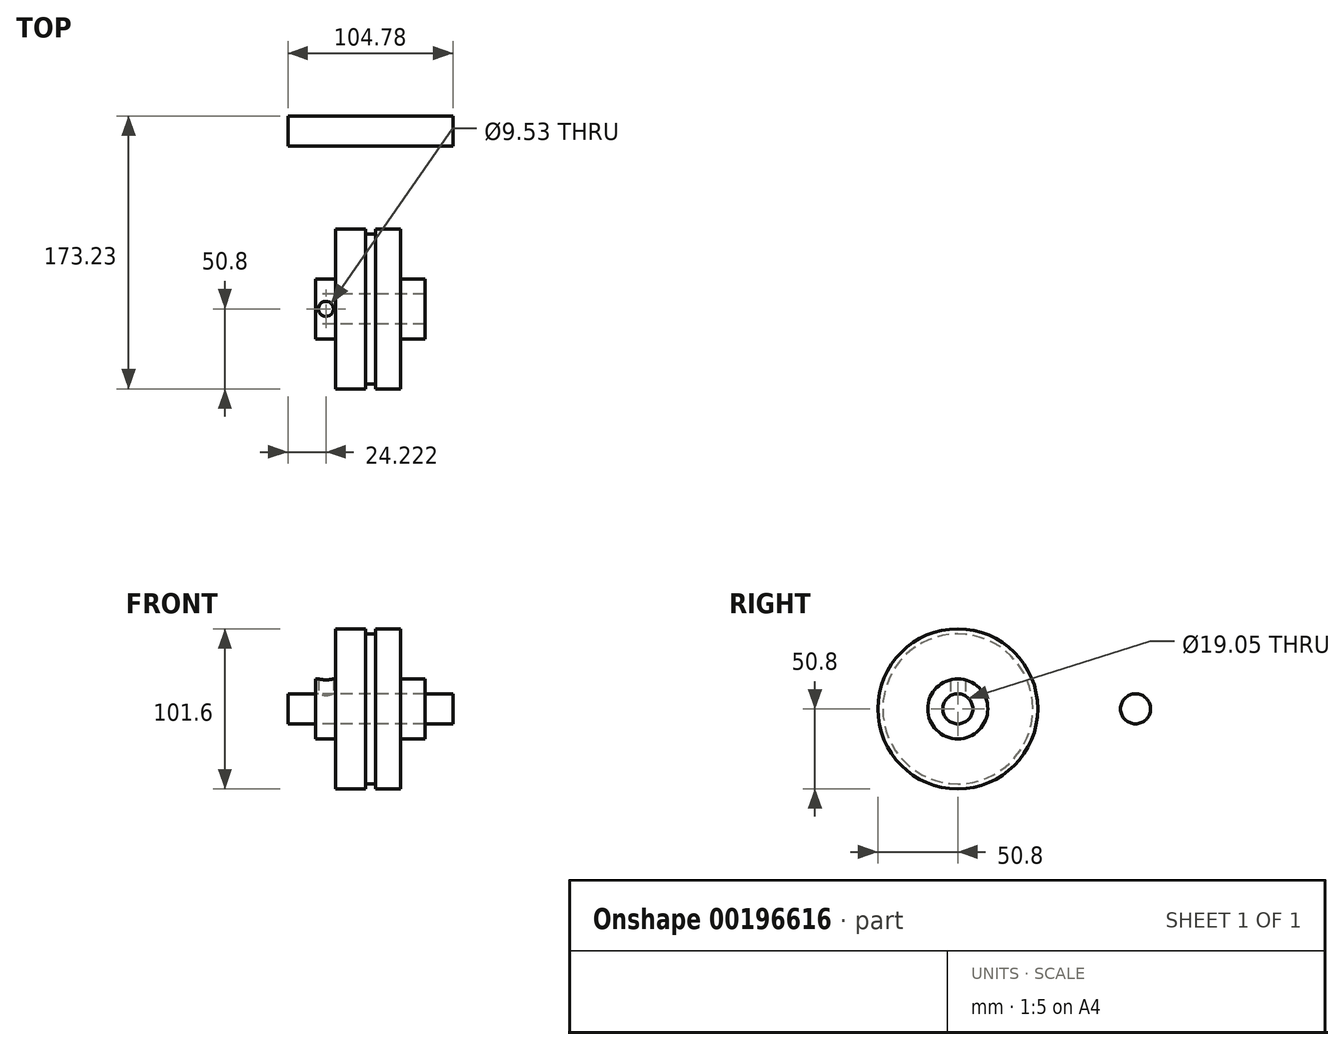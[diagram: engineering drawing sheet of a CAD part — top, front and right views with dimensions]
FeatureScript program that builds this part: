
annotation { "Feature Type Name" : "Feature", "Feature Type Description" : "" }
export const myFeature = defineFeature(function(context is Context, id is Id, definition is map)
    precondition{}
    {
        {
            var Q0;
            Q0=qCreatedBy(makeId("Right.planeOp"),FACE);
            var sketch = newSketch(context, id + "F0", { "sketchPlane" : qUnion([Q0])});
            skCircle(sketch, "E0", {"center": v(0, 0) * mm, "radius": 9.53 * mm});
            skCircle(sketch, "E1", {"center": v(0, 0) * mm, "radius": 19.05 * mm});
            skSolve(sketch);
        }
        {
            var Q0;
            Q0=qCreatedBy(makeId("Right.planeOp"),FACE);
            var sketch = newSketch(context, id + "F1", { "sketchPlane" : qUnion([Q0])});
            skCircle(sketch, "E2", {"center": v(112.9, 0) * mm, "radius": 9.53 * mm});
            skSolve(sketch);
        }
        {
            var Q0;
            Q0=makeQuery(id+"F0.imprint","IMPRINT",FACE,{"disambiguationData":[TD([[makeQuery(id+"F0.imprint","IMPRINT",EDGE,{"derivedFrom":sQuery(id+"F0.wireOp",EDGE,"E0")}),-1.0]])]});
            extrude(context, id + "F2", {"entities" : qUnion([Q0]), "endBound" : BoundingType.SYMMETRIC, "depth" : 69.34 * mm});
        }
        {
            var Q0;
            Q0=qCreatedBy(makeId("Right.planeOp"),FACE);
            var sketch = newSketch(context, id + "F3", { "sketchPlane" : qUnion([Q0])});
            skCircle(sketch, "E3", {"center": v(0, 0) * mm, "radius": 50.8 * mm});
            skCircle(sketch, "E4", {"center": v(0, 0) * mm, "radius": 47.63 * mm});
            skSolve(sketch);
        }
        {
            var Q0;
            Q0=makeQuery(id+"F3.imprint","IMPRINT",FACE,{"disambiguationData":[TD([[makeQuery(id+"F3.imprint","IMPRINT",EDGE,{"derivedFrom":sQuery(id+"F3.wireOp",EDGE,"E4")}),1.0]])]});
            var Q1;
            Q1=makeQuery(id+"F3.imprint","IMPRINT",FACE,{"disambiguationData":[TD([[makeQuery(id+"F3.imprint","IMPRINT",EDGE,{"derivedFrom":sQuery(id+"F3.wireOp",EDGE,"E3")}),1.0]])]});
            extrude(context, id + "F4", {"entities" : qUnion([Q0, Q1]), "operationType" : NewBodyOperationType.ADD, "endBound" : BoundingType.SYMMETRIC, "depth" : 44.45 * mm});
        }
        {
            var Q0;
            Q0=makeQuery(id+"F4.boolean.opBoolean","SPLIT",FACE,{"disambiguationData":[TD([makeQuery(id+"F2.opExtrude","SWEPT_FACE",FACE,{"disambiguationData":[OSD([sQuery(id+"F0.wireOp",EDGE,"E0")])]})])],"derivedFrom":makeQuery(id+"F4.opExtrude","CAP_FACE",FACE,{"disambiguationData":[OSD([sQuery(id+"F3.wireOp",EDGE,"E3")])],"isStart":false})});
            extrude(context, id + "F5", {"entities" : qUnion([Q0]), "operationType" : NewBodyOperationType.REMOVE, "endBound" : BoundingType.THROUGH_ALL, "oppositeDirection" : true, "depth" : 25.4 * mm});
        }
        {
            var Q0;
            Q0 = qSketchRegion(id + "F3", true);
            var Q1;
            {var subQ0=sQuery(id+"F3.wireOp",EDGE,"E3");Q1=makeQuery(id+"F4.boolean.opBoolean","SPLIT",FACE,{"disambiguationData":[TD([makeQuery(id+"F2.opExtrude","SWEPT_FACE",FACE,{"disambiguationData":[OSD([sQuery(id+"F0.wireOp",EDGE,"E1")])]})])],"derivedFrom":makeQuery(id+"F4.opExtrude","CAP_FACE",FACE,{"disambiguationData":[OSD([subQ0])],"isStart":false})});}
            extrude(context, id + "F6", {"entities" : qUnion([Q0, Q1]), "operationType" : NewBodyOperationType.REMOVE, "endBound" : BoundingType.SYMMETRIC, "oppositeDirection" : true, "depth" : 6.35 * mm});
        }
        {
            var Q0;
            Q0=qCreatedBy(makeId("Top.planeOp"),FACE);
            var sketch = newSketch(context, id + "F7", { "sketchPlane" : qUnion([Q0])});
            skCircle(sketch, "E5", {"center": v(-28.17, 0) * mm, "radius": 4.76 * mm});
            skSolve(sketch);
        }
        {
            var Q0;
            Q0 = qSketchRegion(id + "F7", true);
            extrude(context, id + "F8", {"entities" : qUnion([Q0]), "operationType" : NewBodyOperationType.REMOVE, "depth" : 25.4 * mm});
        }
        {
            var Q0;
            Q0=makeQuery(id+"F1.imprint","IMPRINT",FACE,{"disambiguationData":[TD([[makeQuery(id+"F1.imprint","IMPRINT",EDGE,{"derivedFrom":sQuery(id+"F1.wireOp",EDGE,"E2")}),1.0]])]});
            extrude(context, id + "F9", {"entities" : qUnion([Q0]), "endBound" : BoundingType.SYMMETRIC, "depth" : 104.77 * mm});
        }
    });
